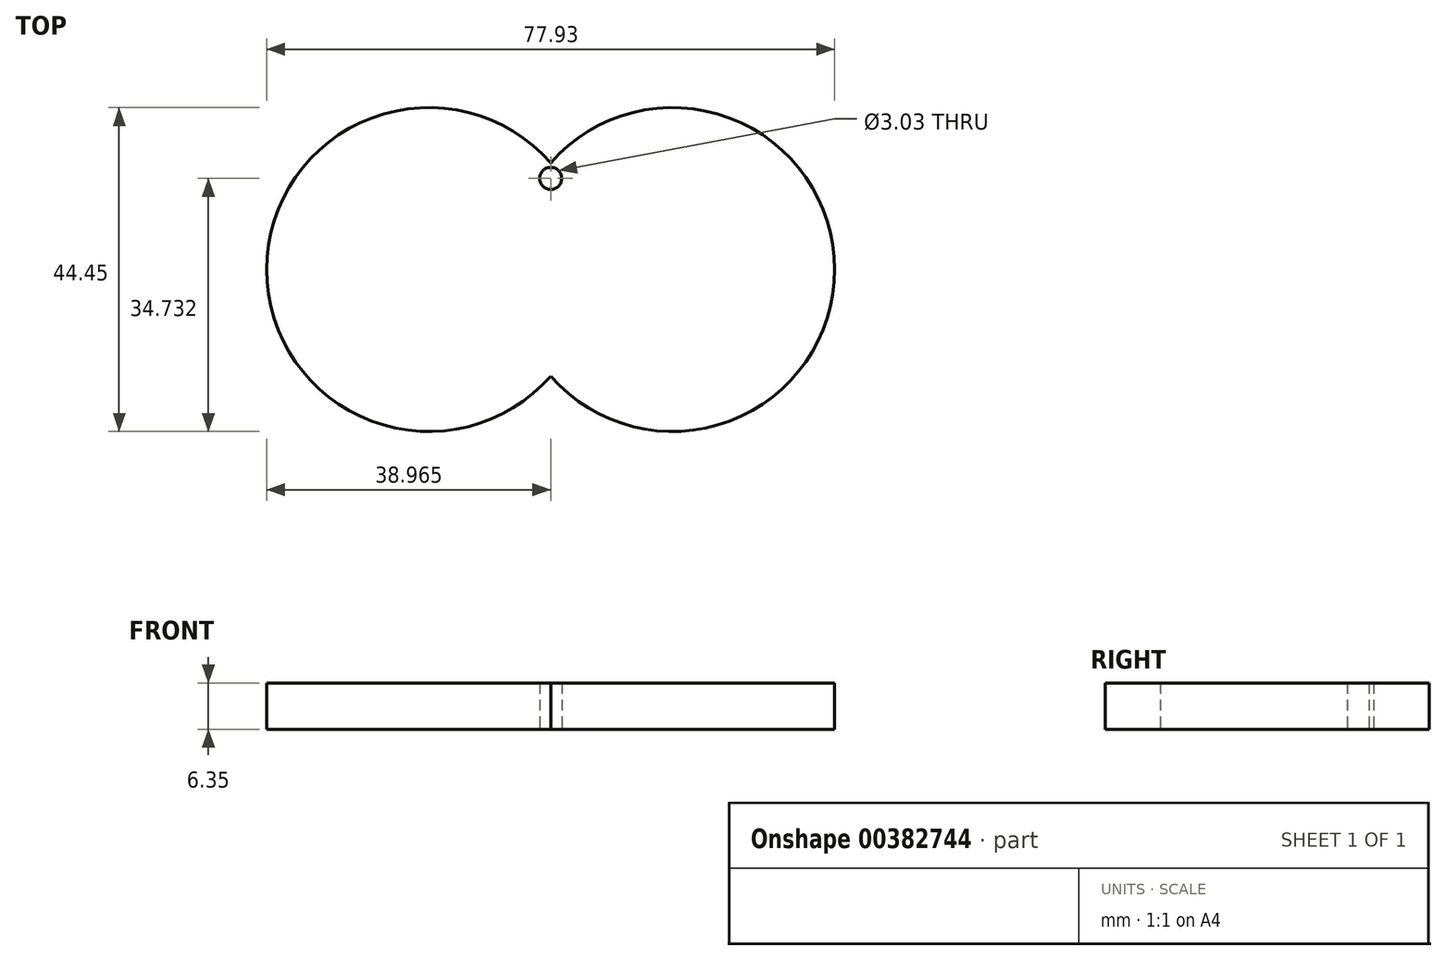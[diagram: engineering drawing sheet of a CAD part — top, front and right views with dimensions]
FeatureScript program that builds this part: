
annotation { "Feature Type Name" : "Feature", "Feature Type Description" : "" }
export const myFeature = defineFeature(function(context is Context, id is Id, definition is map)
    precondition{}
    {
        {
            var Q0;
            Q0=qCreatedBy(makeId("Top.planeOp"),FACE);
            var sketch = newSketch(context, id + "F0", { "sketchPlane" : qUnion([Q0])});
            skArc(sketch, "E0", {"start": v(-25.85, 33.48) * mm, "mid": v(13.1, 48.1) * mm, "end": v(-25.85, 62.73) * mm});
            skArc(sketch, "E1", {"start": v(-25.85, 62.73) * mm, "mid": v(-64.82, 48.1) * mm, "end": v(-25.85, 33.48) * mm});
            skArc(sketch, "E2.0", {"start": v(-25.85, 51.82) * mm, "mid": v(-59.74, 48.1) * mm, "end": v(-25.85, 44.4) * mm});
            skArc(sketch, "E2.1", {"start": v(-25.85, 44.4) * mm, "mid": v(8.03, 48.1) * mm, "end": v(-25.85, 51.82) * mm});
            skLineSegment(sketch, "E3", {"start": v(-25.85, 62.73) * mm, "end": v(-25.85, 51.82) * mm, "construction": true});
            skCircle(sketch, "E4", {"center": v(-25.85, 60.61) * mm, "radius": 1.52 * mm});
            skSolve(sketch);
        }
        {
            var Q0;
            Q0 = qSketchRegion(id + "F0", true);
            var Q1;
            Q1=makeQuery(id+"F0.imprint","IMPRINT",FACE,{"disambiguationData":[TD([[makeQuery(id+"F0.imprint","IMPRINT",EDGE,{"derivedFrom":sQuery(id+"F0.wireOp",EDGE,"E2.0")}),1.0]])]});
            extrude(context, id + "F1", {"entities" : qUnion([Q0, Q1]), "depth" : 6.35 * mm});
        }
    });
